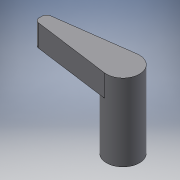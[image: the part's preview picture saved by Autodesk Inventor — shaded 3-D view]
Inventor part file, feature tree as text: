
AUTODESK INVENTOR PART (.ipt)
format: ipt  version: 2019 (Build 230136000, 136)  size: 109,568 bytes
history: native  units: in
note: dims shown in document units (in); Inventor stores cm internally (conversion verified against a paired STEP export)
features: extrude x2, sketch x2, fillet x1
ambient origin geometry x8: Origin, YZ Plane, XZ Plane, XY Plane, X Axis, Y Axis, Z Axis, Center Point
bodies: Solid1 (feature_tree)
feature tree (5):
  extrude  "Extrusion1"  Depth=0.0787in
  extrude  "Extrusion2"  Depth=0.0157in
  fillet  "Fillet1"  Radius=0.0394in
  sketch  "Sketch1"  dims[d0=0.0787in d1=0.0in d2=0.1181in]
  sketch  "Sketch2"  dims[d11=0.1969in d12=0.0in d13=0.2953in d14=0.0394in d15=0.0157in]
